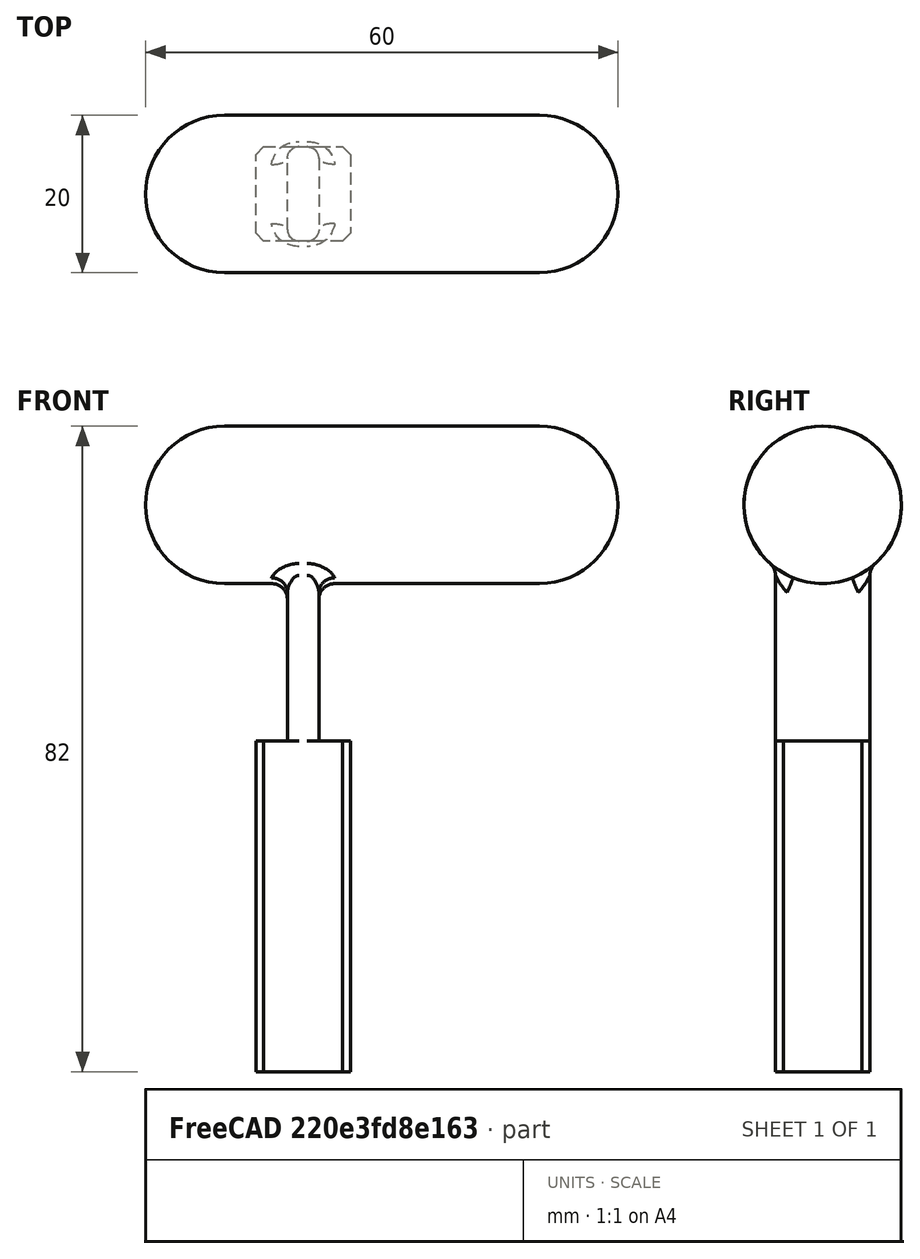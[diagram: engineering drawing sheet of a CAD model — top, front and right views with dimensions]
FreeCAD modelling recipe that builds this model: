
FCSTD DOCUMENT  (FreeCAD 0.21R33771 (Git))
Label: stamp
License: All rights reserved
LicenseURL: http://en.wikipedia.org/wiki/All_rights_reserved
objects: Sketcher::SketchObject×3, PartDesign::Pad×3, PartDesign::Fillet×3, PartDesign::Chamfer×1, PartDesign::Body×1, Mesh::Feature×1
note: 18 computed .brp shape members not serialized (recipe doc carries the construction recipe); baked Part::Feature solids carry a one-line shape summary decoded from their .brp

FEATURE [Sketcher::SketchObject] Sketch
  FullyConstrained = true
  MapMode = 5
  Support = -> [XY_Plane]
  sketch-geometry (6):
    g0: LineSegment StartX=-6 StartY=6 StartZ=0 EndX=6 EndY=6 EndZ=0
    g1: LineSegment StartX=6 StartY=6 StartZ=0 EndX=6 EndY=-6 EndZ=0
    g2: LineSegment StartX=6 StartY=-6 StartZ=0 EndX=-6 EndY=-6 EndZ=0
    g3: LineSegment StartX=-6 StartY=-6 StartZ=0 EndX=-6 EndY=6 EndZ=0
    g4: LineSegment StartX=-6 StartY=6 StartZ=0 EndX=6 EndY=-6 EndZ=0
    g5: LineSegment StartX=6 StartY=6 StartZ=0 EndX=-6 EndY=-6 EndZ=0
  constraints (16):
    c: Coincident(g0,g1)
    c: Coincident(g1,g2)
    c: Coincident(g2,g3)
    c: Coincident(g3,g0)
    c: Horizontal(g0)
    c: Horizontal(g2)
    c: Vertical(g1)
    c: Vertical(g3)
    c: Coincident(g4,g0)
    c: Coincident(g4,g1)
    c: PointOnObject(g-1,g4)
    c: Distance(g0) = 12
    c: Equal(g1,g0)
    c: Coincident(g5,g0)
    c: Coincident(g5,g2)
    c: PointOnObject(g-1,g5)
FEATURE [PartDesign::Pad] Pad
  Direction = (0,0,1)
  Length = 42
  Length2 = 10
  Profile = -> Sketch
  ReferenceAxis = -> Sketch [N_Axis]
  Type = 0
  expr: Length = 12 * 3 + 6
FEATURE [Sketcher::SketchObject] Sketch001
  ExternalGeometry = -> [Pad]
  FullyConstrained = true
  MapMode = 5
  Placement = pos=(0,0,42) rot=(0,0,1;0rad)
  Support = -> [Pad]
  sketch-geometry (5):
    g0: LineSegment StartX=-2 StartY=6 StartZ=0 EndX=2 EndY=6 EndZ=0
    g1: LineSegment StartX=2 StartY=6 StartZ=0 EndX=2 EndY=-6 EndZ=0
    g2: LineSegment StartX=2 StartY=-6 StartZ=0 EndX=-2 EndY=-6 EndZ=0
    g3: LineSegment StartX=-2 StartY=-6 StartZ=0 EndX=-2 EndY=6 EndZ=0
    g4: LineSegment StartX=-2 StartY=-6 StartZ=0 EndX=2 EndY=6 EndZ=0
  constraints (14):
    c: Coincident(g0,g1)
    c: Coincident(g1,g2)
    c: Coincident(g2,g3)
    c: Coincident(g3,g0)
    c: Horizontal(g0)
    c: Horizontal(g2)
    c: Vertical(g1)
    c: Vertical(g3)
    c: PointOnObject(g0,g-3)
    c: PointOnObject(g1,g-4)
    c: Coincident(g4,g2)
    c: Coincident(g4,g0)
    c: PointOnObject(g-1,g4)
    c: Distance(g2) = 4
FEATURE [PartDesign::Pad] Pad001
  BaseFeature = -> Pad
  Direction = (0,0,1)
  Length = 30
  Length2 = 10
  Profile = -> Sketch001
  ReferenceAxis = -> Sketch001 [N_Axis]
  Type = 0
FEATURE [Sketcher::SketchObject] Sketch002
  ExternalGeometry = -> [Pad001]
  FullyConstrained = true
  MapMode = 5
  Placement = pos=(0,0,0) rot=(0.57735,0.57735,0.57735;2.0944rad)
  Support = -> [YZ_Plane]
  sketch-geometry (2):
    g0: LineSegment StartX=0 StartY=72 StartZ=0 EndX=10 EndY=72 EndZ=0
    g1: Circle CenterX=0 CenterY=72 CenterZ=0 NormalX=0 NormalY=0 NormalZ=1 AngleXU=0 Radius=10
  constraints (6):
    c: PointOnObject(g0,g-2)
    c: Horizontal(g0)
    c: PointOnObject(g0,g-3)
    c: Coincident(g1,g0)
    c: PointOnObject(g0,g1)
    c: Distance(g0) = 10
FEATURE [PartDesign::Pad] Pad002
  BaseFeature = -> Pad001
  Direction = (1,-2e-16,3e-16)
  Length = 40
  Length2 = 20
  Profile = -> Sketch002
  ReferenceAxis = -> Sketch002 [N_Axis]
  Type = 4
FEATURE [PartDesign::Chamfer] Chamfer
  Angle = 45
  Base = -> Pad002 [Edge10,Edge7,Edge1,Edge2]
  BaseFeature = -> Pad002
  ChamferType = 0
  FlipDirection = false
  Size = 1
  Size2 = 1
  SupportTransform = false
  UseAllEdges = false
FEATURE [PartDesign::Fillet] Fillet
  Base = -> Chamfer [Edge36,Edge35,Edge26,Edge28]
  BaseFeature = -> Chamfer
  Radius = 1.5
  SupportTransform = false
  UseAllEdges = false
FEATURE [PartDesign::Fillet] Fillet001
  Base = -> Fillet [Edge40]
  BaseFeature = -> Fillet
  Radius = 2
  SupportTransform = false
  UseAllEdges = false
FEATURE [PartDesign::Fillet] Fillet002
  Base = -> Fillet001 [Edge34,Edge32]
  BaseFeature = -> Fillet001
  Radius = 10
  SupportTransform = false
  UseAllEdges = false
FEATURE [PartDesign::Body] Body
  Group = -> [Sketch,Pad,Sketch001,Pad001,Sketch002,Pad002,Chamfer,Fillet,Fillet001,Fillet002]
  Origin = -> Origin
  Tip = -> Fillet002
FEATURE [Mesh::Feature] Mesh001  label="print-stamp"
